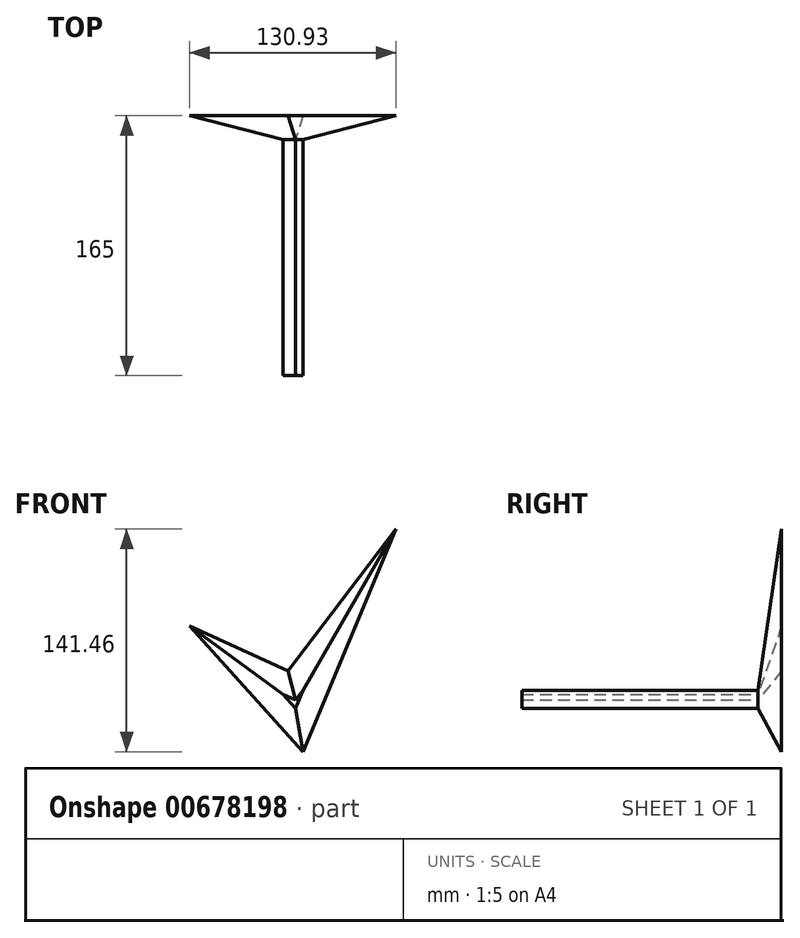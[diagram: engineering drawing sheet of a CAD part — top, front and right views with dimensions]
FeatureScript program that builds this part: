
annotation { "Feature Type Name" : "Feature", "Feature Type Description" : "" }
export const myFeature = defineFeature(function(context is Context, id is Id, definition is map)
    precondition{}
    {
        {
            var Q0;
            Q0=qCreatedBy(makeId("Front.planeOp"),FACE);
            var sketch = newSketch(context, id + "F0", { "sketchPlane" : qUnion([Q0])});
            skLineSegment(sketch, "E0", {"start": v(0.78, -1.18) * mm, "end": v(5.55, 5.11) * mm});
            skLineSegment(sketch, "E1", {"start": v(5.55, 5.11) * mm, "end": v(0.78, -6.34) * mm});
            skLineSegment(sketch, "E2", {"start": v(0.78, -6.34) * mm, "end": v(-7.1, 2.4) * mm});
            skLineSegment(sketch, "E3", {"start": v(-7.1, 2.4) * mm, "end": v(0.78, -1.18) * mm});
            skSolve(sketch);
        }
        {
            var Q0;
            Q0=makeQuery(id+"F0.imprint","IMPRINT",FACE,{"disambiguationData":[TD([[makeQuery(id+"F0.imprint","IMPRINT",EDGE,{"derivedFrom":sQuery(id+"F0.wireOp",EDGE,"E0")}),-1.0]])]});
            var Q1;
            Q1=sQuery(id+"F0.wireOp",EDGE,"E0");
            var Q2;
            Q2=sQuery(id+"F0.wireOp",EDGE,"E1");
            var Q3;
            Q3=sQuery(id+"F0.wireOp",EDGE,"E2");
            var Q4;
            Q4=sQuery(id+"F0.wireOp",EDGE,"E3");
            extrude(context, id + "F1", {"entities" : qUnion([Q0]), "surfaceEntities" : qUnion([Q1, Q2, Q3, Q4]), "depth" : 150 * mm, "offsetDistance" : 25 * mm});
        }
        {
            var Q0;
            Q0=makeQuery(id+"F1.opExtrude","CAP_FACE",FACE,{"disambiguationData":[OSD([sQuery(id+"F0.wireOp",EDGE,"E0"),sQuery(id+"F0.wireOp",EDGE,"E1"),sQuery(id+"F0.wireOp",EDGE,"E2"),sQuery(id+"F0.wireOp",EDGE,"E3")])],"isStart":true});
            extrude(context, id + "F2", {"entities" : qUnion([Q0]), "operationType" : NewBodyOperationType.ADD, "depth" : 15 * mm, "offsetDistance" : 25 * mm, "hasDraft" : true, "draftAngle" : 45 * degree});
        }
    });
